# Revit family: ПУ_18.01.2022
name_source: partatom
category: Оборудование
units: mm (PartAtom-declared; Revit-internal decimal feet)

## family parameters
Всегда вертикально = Да
Классификация = Нет
На основе рабочей плоскости = Нет
Общий = Нет
При загрузке вырезать с полостями = Нет
Размер круглого соединителя = Использовать диаметр
Тип детали = Нормальный
Точка расчета площади = Нет

## types (1)
- ПУ
    Изготовитель = Плазма-Т
    Изображение типоразмера = ПУ.png
    Ключевая пометка = ПАНЕЛЬ управления АВУЮ 634.211.021
    Надпись ПУ = Да
    Описание = ПУ предназначена для:

автоматического управления оборудованием пожаротушения (водяного, пенного, газового, порошкового, аэрозольного);
автоматического управления дымоудалением и вентиляцией;
автоматического управления оповещением;
автоматического управления технологическим оборудованием (в том числе насосами холодного водоснабжения, горячего водоснабжения, циркуляции отопления, подпитки отопления, дренажа);
работы в качестве пожарной сигнализации с безадресными извещателями;
работы в составе СПАС «СПРУТ-2».
водоснабжения, горячего водоснабжения, циркуляции отопления, подпитки отопления, дренажа); работы в качестве пожарной сигнализации с безадресными извещателями; работы с комплектом «Спрут-2»
    Отметка по умолчанию = 0 мм
